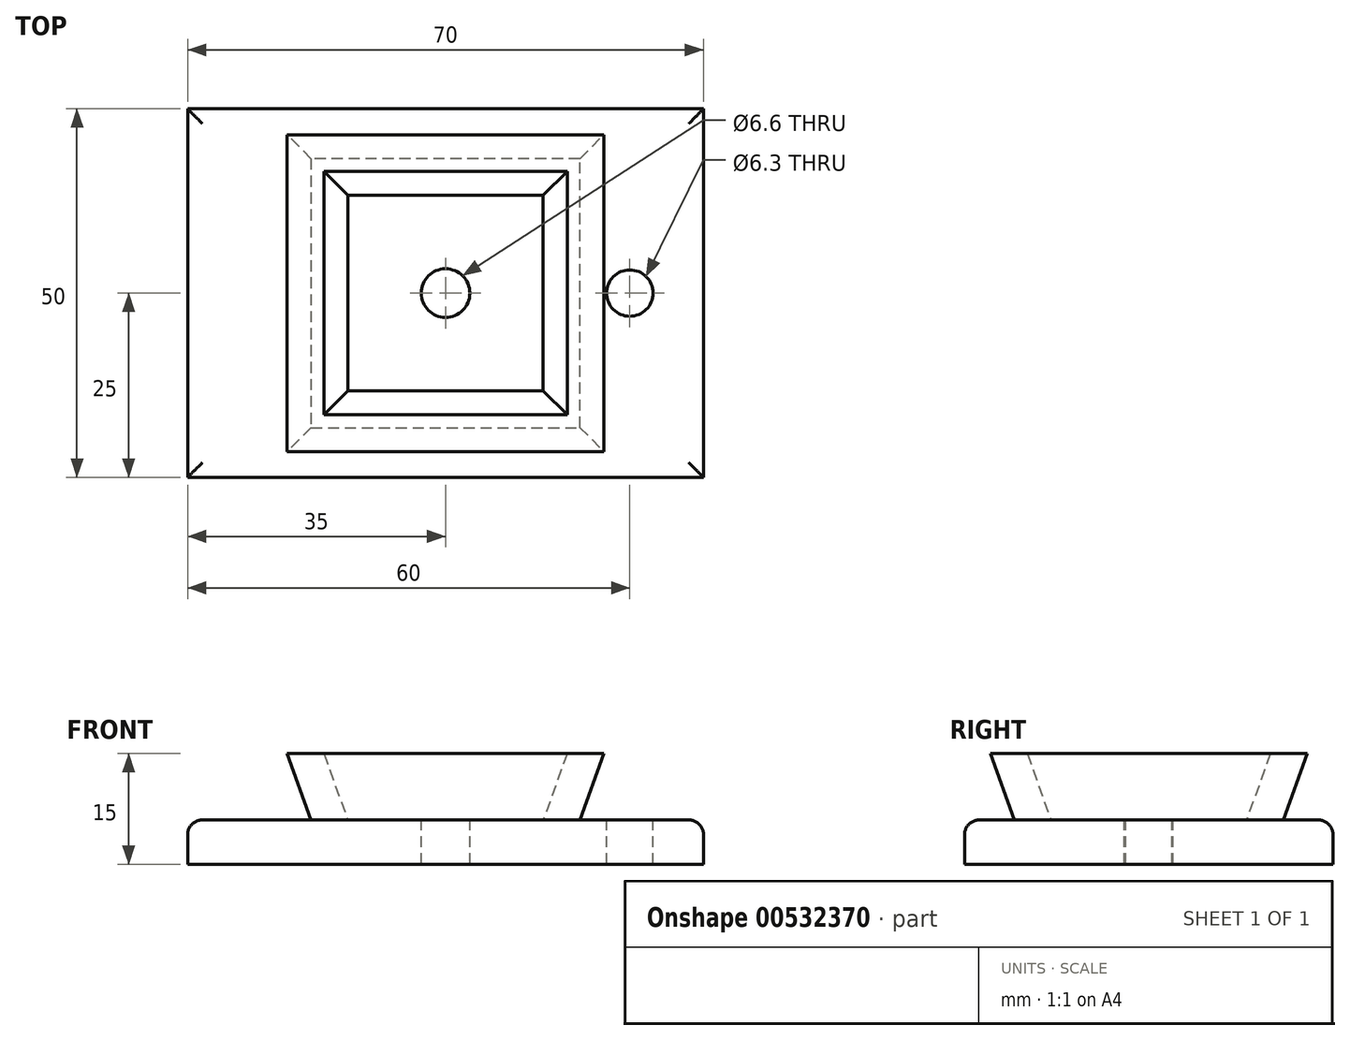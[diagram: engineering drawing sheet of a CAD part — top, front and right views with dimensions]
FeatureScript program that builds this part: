
annotation { "Feature Type Name" : "Feature", "Feature Type Description" : "" }
export const myFeature = defineFeature(function(context is Context, id is Id, definition is map)
    precondition{}
    {
        {
            var Q0;
            Q0=qCreatedBy(makeId("Top.planeOp"),FACE);
            var sketch = newSketch(context, id + "F0", { "sketchPlane" : qUnion([Q0])});
            skLineSegment(sketch, "E0.bottom", {"start": v(35, -25) * mm, "end": v(-35, -25) * mm});
            skLineSegment(sketch, "E0.top", {"start": v(35, 25) * mm, "end": v(-35, 25) * mm});
            skLineSegment(sketch, "E0.left", {"start": v(35, -25) * mm, "end": v(35, 25) * mm});
            skLineSegment(sketch, "E0.right", {"start": v(-35, -25) * mm, "end": v(-35, 25) * mm});
            skPoint(sketch, "E0.middle", {"position": v(0, 0) * mm});
            skSolve(sketch);
        }
        {
            var Q0;
            Q0 = qSketchRegion(id + "F0", true);
            extrude(context, id + "F1", {"entities" : qUnion([Q0]), "depth" : 6 * mm, "offsetDistance" : 25 * mm});
        }
        {
            var Q0;
            Q0=makeQuery(id+"F1.opExtrude","CAP_FACE",FACE,{"disambiguationData":[OSD([sQuery(id+"F0.wireOp",EDGE,"E0.bottom"),sQuery(id+"F0.wireOp",EDGE,"E0.top"),sQuery(id+"F0.wireOp",EDGE,"E0.left"),sQuery(id+"F0.wireOp",EDGE,"E0.right")])],"isStart":false});
            var sketch = newSketch(context, id + "F2", { "sketchPlane" : qUnion([Q0])});
            skLineSegment(sketch, "E1.bottom", {"start": v(18.25, -18.25) * mm, "end": v(-18.25, -18.25) * mm});
            skLineSegment(sketch, "E1.top", {"start": v(18.25, 18.25) * mm, "end": v(-18.25, 18.25) * mm});
            skLineSegment(sketch, "E1.left", {"start": v(18.25, -18.25) * mm, "end": v(18.25, 18.25) * mm});
            skLineSegment(sketch, "E1.right", {"start": v(-18.25, -18.25) * mm, "end": v(-18.25, 18.25) * mm});
            skPoint(sketch, "E1.middle", {"position": v(0, 0) * mm});
            skSolve(sketch);
        }
        {
            var Q0;
            Q0=qCreatedBy(makeId("Right.planeOp"),FACE);
            var sketch = newSketch(context, id + "F3", { "sketchPlane" : qUnion([Q0])});
            skLineSegment(sketch, "E2", {"start": v(-18.25, 6) * mm, "end": v(-21.5, 15) * mm});
            skLineSegment(sketch, "E3", {"start": v(-21.5, 15) * mm, "end": v(-16.5, 15) * mm});
            skLineSegment(sketch, "E4", {"start": v(-16.5, 15) * mm, "end": v(-13.25, 6) * mm});
            skLineSegment(sketch, "E5", {"start": v(-13.25, 6) * mm, "end": v(-18.25, 6) * mm});
            skSolve(sketch);
        }
        {
            var Q0;
            Q0=makeQuery(id+"F3.imprint","IMPRINT",FACE,{"disambiguationData":[TD([[makeQuery(id+"F3.imprint","IMPRINT",EDGE,{"derivedFrom":sQuery(id+"F3.wireOp",EDGE,"E2")}),-1.0]])]});
            var Q1;
            Q1=sQuery(id+"F2.wireOp",EDGE,"E1.bottom");
            var Q2;
            Q2=sQuery(id+"F2.wireOp",EDGE,"E1.left");
            var Q3;
            Q3=sQuery(id+"F2.wireOp",EDGE,"E1.top");
            var Q4;
            Q4=sQuery(id+"F2.wireOp",EDGE,"E1.right");
            sweep(context, id + "F4", {"operationType" : NewBodyOperationType.ADD, "profiles" : qUnion([Q0]), "path" : qUnion([Q1, Q2, Q3, Q4])});
        }
        {
            var Q0;
            Q0=makeQuery(id+"F2.imprint","IMPRINT",FACE,{"disambiguationData":[TD([[makeQuery(id+"F2.imprint","IMPRINT",EDGE,{"derivedFrom":sQuery(id+"F2.wireOp",EDGE,"E1.bottom")}),1.0]])]});
            var sketch = newSketch(context, id + "F5", { "sketchPlane" : qUnion([Q0])});
            skCircle(sketch, "E6", {"center": v(0, 0) * mm, "radius": 3.3 * mm});
            skSolve(sketch);
        }
        {
            var Q0;
            Q0 = qSketchRegion(id + "F5", true);
            var Q1;
            Q1=makeQuery(id+"F1.opExtrude","CAP_FACE",FACE,{"disambiguationData":[OSD([sQuery(id+"F0.wireOp",EDGE,"E0.bottom"),sQuery(id+"F0.wireOp",EDGE,"E0.top"),sQuery(id+"F0.wireOp",EDGE,"E0.left"),sQuery(id+"F0.wireOp",EDGE,"E0.right")])],"isStart":true});
            extrude(context, id + "F6", {"entities" : qUnion([Q0]), "operationType" : NewBodyOperationType.REMOVE, "endBound" : BoundingType.UP_TO_SURFACE, "oppositeDirection" : true, "depth" : 25 * mm, "endBoundEntityFace" : qUnion([Q1]), "offsetDistance" : 25 * mm});
        }
        {
            var Q0;
            Q0=makeQuery(id+"F1.opExtrude","CAP_EDGE",EDGE,{"disambiguationData":[OSD([sQuery(id+"F0.wireOp",EDGE,"E0.left")])],"isStart":false});
            var Q1;
            Q1=makeQuery(id+"F1.opExtrude","CAP_EDGE",EDGE,{"disambiguationData":[OSD([sQuery(id+"F0.wireOp",EDGE,"E0.top")])],"isStart":false});
            var Q2;
            Q2=makeQuery(id+"F1.opExtrude","CAP_EDGE",EDGE,{"disambiguationData":[OSD([sQuery(id+"F0.wireOp",EDGE,"E0.right")])],"isStart":false});
            var Q3;
            Q3=makeQuery(id+"F1.opExtrude","CAP_EDGE",EDGE,{"disambiguationData":[OSD([sQuery(id+"F0.wireOp",EDGE,"E0.bottom")])],"isStart":false});
            fillet(context, id + "F7", {"entities" : qUnion([Q0, Q1, Q2, Q3]), "radius" : 2 * mm, "tangentPropagation" : true, "allowEdgeOverflow" : false});
        }
        {
            var Q0;
            Q0=makeQuery(id+"F2.imprint","IMPRINT",FACE,{"disambiguationData":[TD([[makeQuery(id+"F2.imprint","IMPRINT",EDGE,{"derivedFrom":sQuery(id+"F2.wireOp",EDGE,"E1.bottom")}),1.0]])]});
            var sketch = newSketch(context, id + "F8", { "sketchPlane" : qUnion([Q0])});
            skCircle(sketch, "E7", {"center": v(25, 0) * mm, "radius": 3.15 * mm});
            skSolve(sketch);
        }
        {
            var Q0;
            Q0=makeQuery(id+"F8.imprint","IMPRINT",FACE,{"disambiguationData":[TD([[makeQuery(id+"F8.imprint","IMPRINT",EDGE,{"derivedFrom":sQuery(id+"F8.wireOp",EDGE,"E7")}),1.0]])]});
            extrude(context, id + "F9", {"entities" : qUnion([Q0]), "operationType" : NewBodyOperationType.REMOVE, "endBound" : BoundingType.UP_TO_NEXT, "oppositeDirection" : true, "depth" : 25 * mm, "offsetDistance" : 25 * mm});
        }
    });
